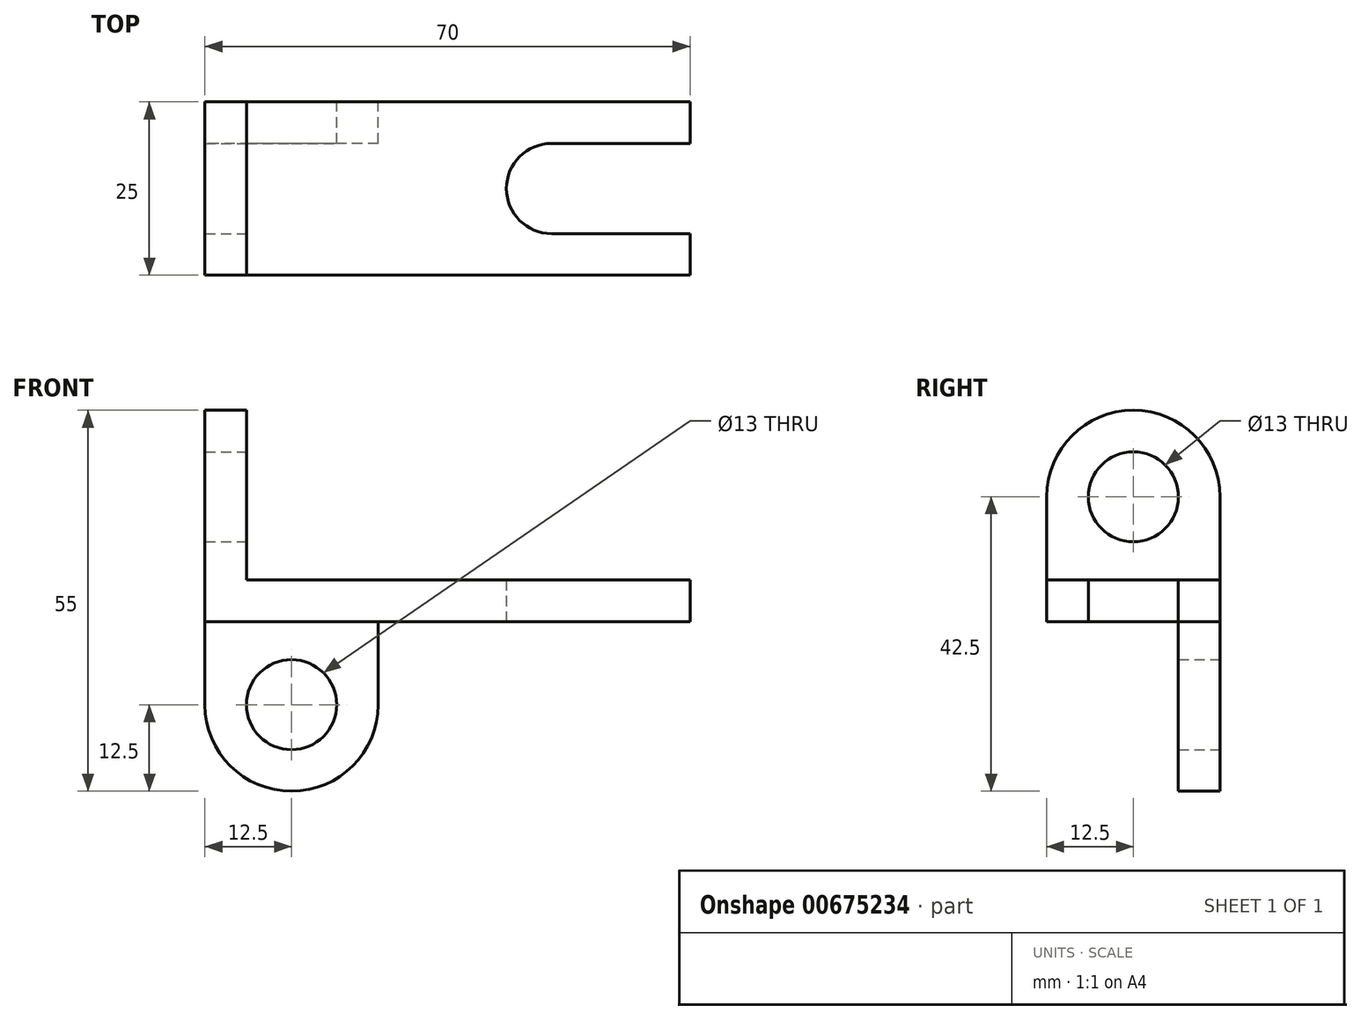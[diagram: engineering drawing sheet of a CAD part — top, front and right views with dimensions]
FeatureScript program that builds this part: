
annotation { "Feature Type Name" : "Feature", "Feature Type Description" : "" }
export const myFeature = defineFeature(function(context is Context, id is Id, definition is map)
    precondition{}
    {
        {
            var Q0;
            Q0=qCreatedBy(makeId("Top.planeOp"),FACE);
            var sketch = newSketch(context, id + "F0", { "sketchPlane" : qUnion([Q0])});
            skLineSegment(sketch, "E0.bottom", {"start": v(32, 12.5) * mm, "end": v(-32, 12.5) * mm});
            skLineSegment(sketch, "E0.top", {"start": v(32, -12.5) * mm, "end": v(-32, -12.5) * mm});
            skLineSegment(sketch, "E0.left", {"start": v(32, 12.5) * mm, "end": v(32, -12.5) * mm});
            skLineSegment(sketch, "E0.right", {"start": v(-32, 12.5) * mm, "end": v(-32, -12.5) * mm});
            skPoint(sketch, "E0.middle", {"position": v(0, 0) * mm});
            skLineSegment(sketch, "E1.bottom", {"start": v(32, 6.5) * mm, "end": v(12, 6.5) * mm});
            skLineSegment(sketch, "E1.top", {"start": v(32, -6.5) * mm, "end": v(12, -6.5) * mm});
            skLineSegment(sketch, "E1.left", {"start": v(32, 6.5) * mm, "end": v(32, -6.5) * mm});
            skLineSegment(sketch, "E1.right", {"start": v(12, 6.5) * mm, "end": v(12, -6.5) * mm});
            skPoint(sketch, "E1.middle", {"position": v(22, 0) * mm});
            skCircle(sketch, "E2", {"center": v(12, 0) * mm, "radius": 6.5 * mm});
            skSolve(sketch);
        }
        {
            var Q0;
            {var subQ4=sQuery(id+"F0.wireOp",EDGE,"E0.bottom");Q0=makeQuery(id+"F0.imprint","IMPRINT",FACE,{"disambiguationData":[TD([[makeQuery(id+"F0.imprint","IMPRINT",EDGE,{"derivedFrom":subQ4}),1.0]])]});}
            extrude(context, id + "F1", {"entities" : qUnion([Q0]), "depth" : 6 * mm, "offsetDistance" : 25 * mm});
        }
        {
            var Q0;
            Q0=makeQuery(id+"F1.opExtrude","SWEPT_FACE",FACE,{"disambiguationData":[OSD([sQuery(id+"F0.wireOp",EDGE,"E0.right")])]});
            var sketch = newSketch(context, id + "F2", { "sketchPlane" : qUnion([Q0])});
            skLineSegment(sketch, "E3.bottom", {"start": v(-12.5, 0) * mm, "end": v(12.5, 0) * mm});
            skLineSegment(sketch, "E3.top", {"start": v(-12.5, 18) * mm, "end": v(-6.5, 18) * mm, "construction": true});
            skLineSegment(sketch, "E3.left", {"start": v(-12.5, 0) * mm, "end": v(-12.5, 18) * mm});
            skLineSegment(sketch, "E3.right", {"start": v(12.5, 0) * mm, "end": v(12.5, 18) * mm});
            skArc(sketch, "E4", {"start": v(12.5, 18) * mm, "mid": v(0, 30.5) * mm, "end": v(-12.5, 18) * mm});
            skCircle(sketch, "E5", {"center": v(0, 18) * mm, "radius": 6.5 * mm});
            skLineSegment(sketch, "E6.trimOffspring", {"start": v(6.5, 18) * mm, "end": v(12.5, 18) * mm, "construction": true});
            skSolve(sketch);
        }
        {
            var Q0;
            {var subQ1=sQuery(id+"F2.wireOp",EDGE,"E3.left");Q0=makeQuery(id+"F2.imprint","IMPRINT",FACE,{"disambiguationData":[TD([[makeQuery(id+"F2.imprint","IMPRINT",EDGE,{"derivedFrom":subQ1}),-1.0]])]});}
            var Q1;
            {var subQ0=sQuery(id+"F2.wireOp",EDGE,"E3.bottom");Q1=makeQuery(id+"F2.imprint","IMPRINT",FACE,{"disambiguationData":[TD([[makeQuery(id+"F2.imprint","IMPRINT",EDGE,{"derivedFrom":subQ0}),1.0]])]});}
            extrude(context, id + "F3", {"entities" : qUnion([Q0, Q1]), "operationType" : NewBodyOperationType.ADD, "depth" : 6 * mm, "offsetDistance" : 25 * mm});
        }
        {
            var Q0;
            Q0=makeQuery(id+"F1.opExtrude","SWEPT_FACE",FACE,{"disambiguationData":[OSD([sQuery(id+"F0.wireOp",EDGE,"E0.bottom")])]});
            var sketch = newSketch(context, id + "F4", { "sketchPlane" : qUnion([Q0])});
            skLineSegment(sketch, "E7.bottom", {"start": v(38, 6) * mm, "end": v(13, 6) * mm});
            skLineSegment(sketch, "E7.top", {"start": v(38, -12) * mm, "end": v(13, -12) * mm});
            skLineSegment(sketch, "E7.left", {"start": v(38, 6) * mm, "end": v(38, -12) * mm});
            skLineSegment(sketch, "E7.right", {"start": v(13, 6) * mm, "end": v(13, -12) * mm});
            skCircle(sketch, "E8", {"center": v(25.5, -12) * mm, "radius": 12.5 * mm});
            skCircle(sketch, "E9", {"center": v(25.5, -12) * mm, "radius": 6.5 * mm});
            skSolve(sketch);
        }
        {
            var Q0;
            Q0 = qSketchRegion(id + "F4", true);
            extrude(context, id + "F5", {"entities" : qUnion([Q0]), "operationType" : NewBodyOperationType.ADD, "oppositeDirection" : true, "depth" : 6 * mm, "offsetDistance" : 25 * mm});
        }
    });
